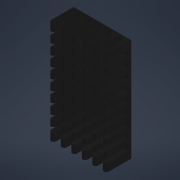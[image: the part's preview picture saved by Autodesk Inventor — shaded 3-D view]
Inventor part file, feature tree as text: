
AUTODESK INVENTOR PART (.ipt)
format: ipt  version: 2021 (Build 250183000, 183)  size: 431,104 bytes
history: native  units: mm
features: extrude x3, sketch x3, other x3, fillet x1, reference x1
ambient origin geometry x8: Origin, YZ Plane, XZ Plane, XY Plane, X Axis, Y Axis, Z Axis, Center Point
bodies: Solid1 (feature_tree)
feature tree (11):
  extrude  "Extrusion1"  Depth=41.0mm
  extrude  "Extrusion2"  Depth=2.0mm
  sketch  "Sketch2"  dims[d2=10.0mm d3=0.0mm d4=2.0mm]
  fillet  "Fillet1"  Radius=3.0mm
  extrude  "Extrusion3"  Depth=3.111111mm
  sketch  "Sketch1"  dims[d0=23.0mm d1=41.0mm]
  reference  "Reference1"
  sketch  "Sketch3"  dims[d5=90.0mm d7=4.111111mm d8=10.0mm d10=10.0mm d12=3.0mm d13=3.111111mm d14=41.0mm d15=60.0mm d17=4.2mm d18=10.0mm d20=10.0mm d22=2.0mm d23=23.0mm d24=10.0mm d25=0.0mm d26=1.0mm d27=1.0mm d28=10.0mm d29=0.0mm d30=3.0mm d31=1.0mm d16=0.872665mm]
  parser-record x1  (decoder bookkeeping rows leaked as tree rows — omitted from the tree; the rows remain in map.json)
  other  "bec.iam"
  other  "board:1"
note: 1 file-system path scrubbed to <path> (originals preserved in map.json)
